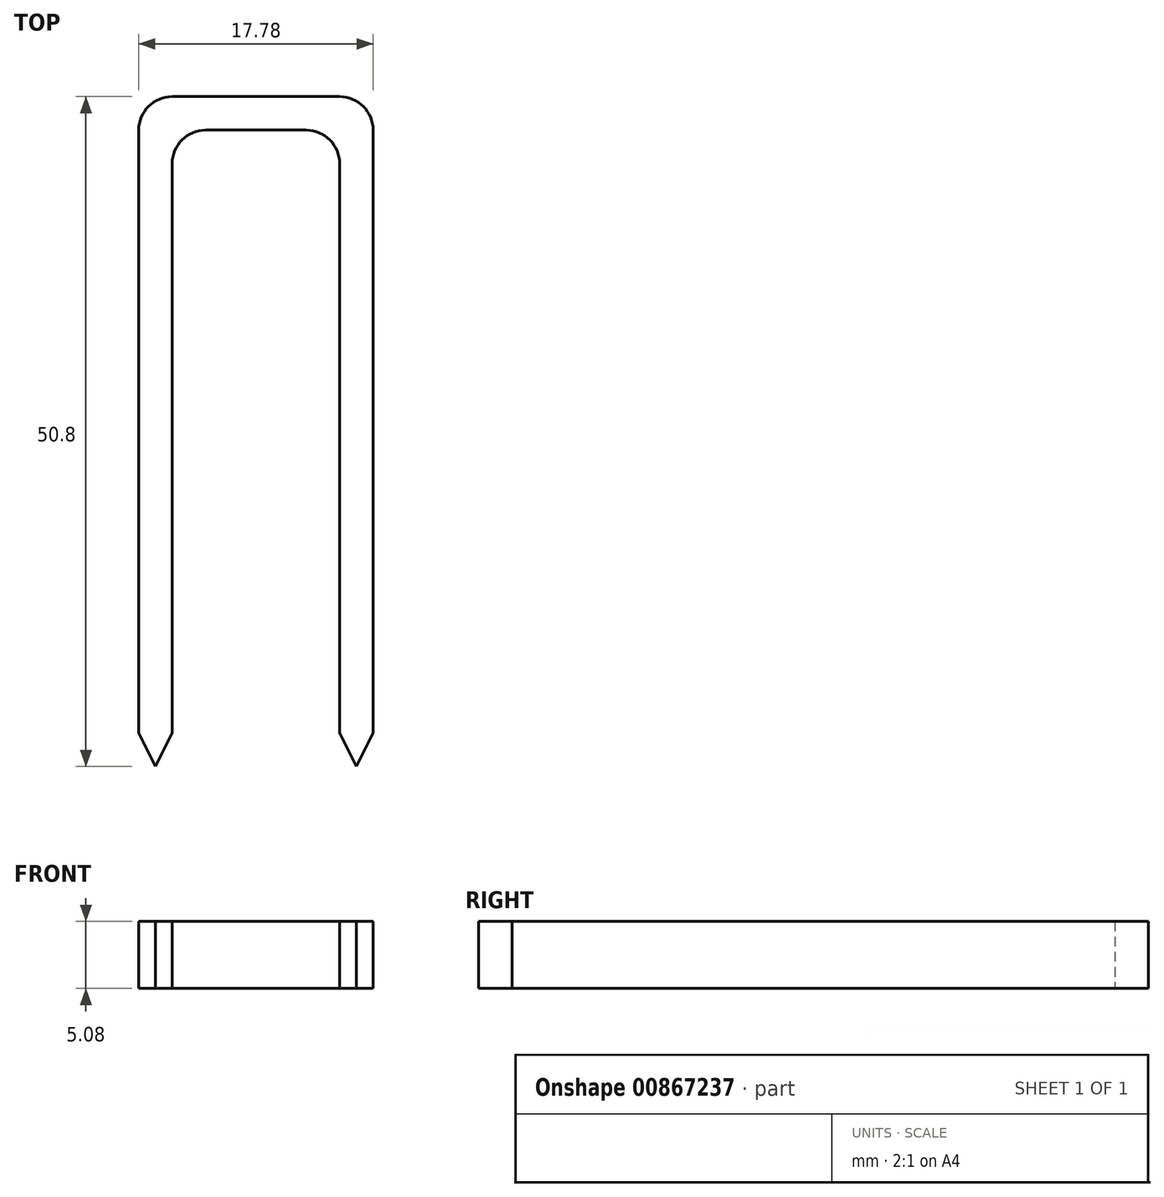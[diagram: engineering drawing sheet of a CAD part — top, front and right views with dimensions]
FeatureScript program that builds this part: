
annotation { "Feature Type Name" : "Feature", "Feature Type Description" : "" }
export const myFeature = defineFeature(function(context is Context, id is Id, definition is map)
    precondition{}
    {
        {
            var Q0;
            Q0=qCreatedBy(makeId("Top.planeOp"),FACE);
            var sketch = newSketch(context, id + "F0", { "sketchPlane" : qUnion([Q0])});
            skLineSegment(sketch, "E0", {"start": v(0, 0) * mm, "end": v(0, 50.8) * mm});
            skLineSegment(sketch, "E1", {"start": v(0, 50.8) * mm, "end": v(17.78, 50.8) * mm});
            skLineSegment(sketch, "E2", {"start": v(17.78, 50.8) * mm, "end": v(17.78, 0) * mm});
            skLineSegment(sketch, "E3", {"start": v(17.78, 0) * mm, "end": v(15.24, 0) * mm});
            skLineSegment(sketch, "E4", {"start": v(15.24, 0) * mm, "end": v(15.24, 48.26) * mm});
            skLineSegment(sketch, "E5", {"start": v(15.24, 48.26) * mm, "end": v(2.54, 48.26) * mm});
            skLineSegment(sketch, "E6", {"start": v(2.54, 48.26) * mm, "end": v(2.54, 0) * mm});
            skLineSegment(sketch, "E7", {"start": v(2.54, 0) * mm, "end": v(0, 0) * mm});
            skLineSegment(sketch, "E8", {"start": v(1.27, 0) * mm, "end": v(2.54, 2.54) * mm});
            skLineSegment(sketch, "E9", {"start": v(1.27, 0) * mm, "end": v(0, 2.54) * mm});
            skLineSegment(sketch, "E10", {"start": v(16.51, 0) * mm, "end": v(17.78, 2.54) * mm});
            skLineSegment(sketch, "E11", {"start": v(16.51, 0) * mm, "end": v(15.24, 2.54) * mm});
            skSolve(sketch);
        }
        {
            var Q0;
            {var subQ4=sQuery(id+"F0.wireOp",EDGE,"E1");Q0=makeQuery(id+"F0.imprint","IMPRINT",FACE,{"disambiguationData":[TD([[makeQuery(id+"F0.imprint","IMPRINT",EDGE,{"derivedFrom":subQ4}),-1.0]])]});}
            extrude(context, id + "F1", {"entities" : qUnion([Q0]), "depth" : 5.08 * mm, "offsetDistance" : 25.4 * mm});
        }
        {
            var Q0;
            Q0=makeQuery(id+"F1.opExtrude","SWEPT_EDGE",EDGE,{"disambiguationData":[OSD([sQuery(id+"F0.wireOp",EDGE,"E5"),sQuery(id+"F0.wireOp",EDGE,"E6")])]});
            var Q1;
            Q1=makeQuery(id+"F1.opExtrude","SWEPT_EDGE",EDGE,{"disambiguationData":[OSD([sQuery(id+"F0.wireOp",EDGE,"E4"),sQuery(id+"F0.wireOp",EDGE,"E5")])]});
            var Q2;
            Q2=makeQuery(id+"F1.opExtrude","SWEPT_EDGE",EDGE,{"disambiguationData":[OSD([sQuery(id+"F0.wireOp",EDGE,"E0"),sQuery(id+"F0.wireOp",EDGE,"E1")])]});
            var Q3;
            Q3=makeQuery(id+"F1.opExtrude","SWEPT_EDGE",EDGE,{"disambiguationData":[OSD([sQuery(id+"F0.wireOp",EDGE,"E1"),sQuery(id+"F0.wireOp",EDGE,"E2")])]});
            fillet(context, id + "F2", {"entities" : qUnion([Q0, Q1, Q2, Q3]), "radius" : 2.54 * mm, "tangentPropagation" : true, "allowEdgeOverflow" : false});
        }
    });
